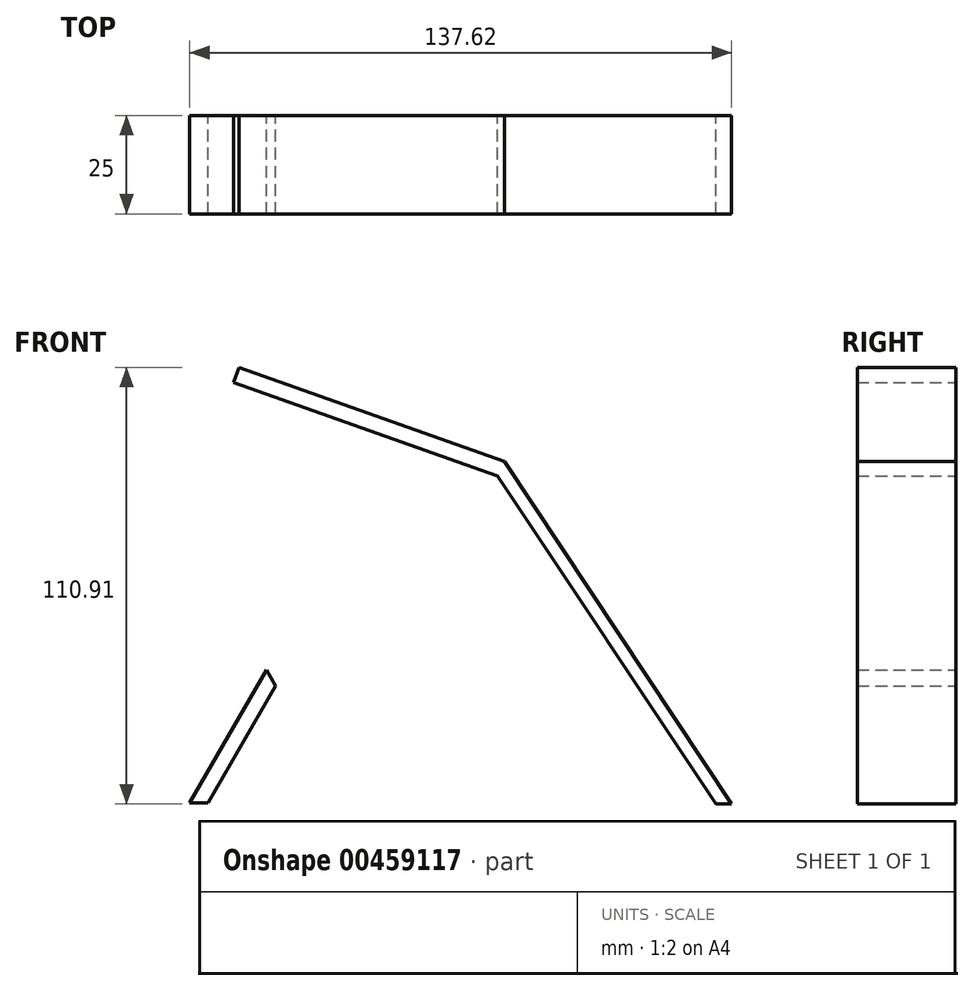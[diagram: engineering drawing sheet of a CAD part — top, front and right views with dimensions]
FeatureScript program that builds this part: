
annotation { "Feature Type Name" : "Feature", "Feature Type Description" : "" }
export const myFeature = defineFeature(function(context is Context, id is Id, definition is map)
    precondition{}
    {
        {
            var Q0;
            Q0=qCreatedBy(makeId("Front.planeOp"),FACE);
            var sketch = newSketch(context, id + "F0", { "sketchPlane" : qUnion([Q0])});
            skLineSegment(sketch, "E0", {"start": v(69.37, -55.21) * mm, "end": v(73.28, -55.21) * mm});
            skLineSegment(sketch, "E1", {"start": v(-59.64, -54.97) * mm, "end": v(-64.34, -54.97) * mm});
            skLineSegment(sketch, "E2", {"start": v(-64.34, -54.97) * mm, "end": v(-46.84, -24.66) * mm});
            skLineSegment(sketch, "E3", {"start": v(-59.64, -54.97) * mm, "end": v(-44.14, -28.13) * mm});
            skLineSegment(sketch, "E4", {"start": v(-64.34, -54.97) * mm, "end": v(-59.64, -54.97) * mm});
            skPoint(sketch, "E5.start.orphan", {"position": v(-74.96, 0) * mm});
            skLineSegment(sketch, "E6", {"start": v(73.28, -55.21) * mm, "end": v(15.58, 31.79) * mm});
            skLineSegment(sketch, "E7", {"start": v(15.58, 31.79) * mm, "end": v(-51.8, 55.7) * mm});
            skLineSegment(sketch, "E8", {"start": v(-51.8, 55.7) * mm, "end": v(-53.16, 51.89) * mm});
            skLineSegment(sketch, "E9", {"start": v(-53.16, 51.89) * mm, "end": v(13.9, 28.1) * mm});
            skLineSegment(sketch, "E10", {"start": v(13.9, 28.1) * mm, "end": v(69.37, -55.21) * mm});
            skLineSegment(sketch, "E11", {"start": v(-64.34, -54.97) * mm, "end": v(-45.54, -22.4) * mm});
            skLineSegment(sketch, "E12", {"start": v(-59.64, -54.97) * mm, "end": v(-42.49, -25.26) * mm});
            skLineSegment(sketch, "E13", {"start": v(-64.34, -54.97) * mm, "end": v(-44.84, -21.2) * mm});
            skLineSegment(sketch, "E14", {"start": v(-44.84, -21.2) * mm, "end": v(-42.49, -25.26) * mm});
            skSolve(sketch);
        }
        {
            var Q0;
            Q0 = qSketchRegion(id + "F0", true);
            extrude(context, id + "F1", {"entities" : qUnion([Q0]), "depth" : 25 * mm});
        }
    });
